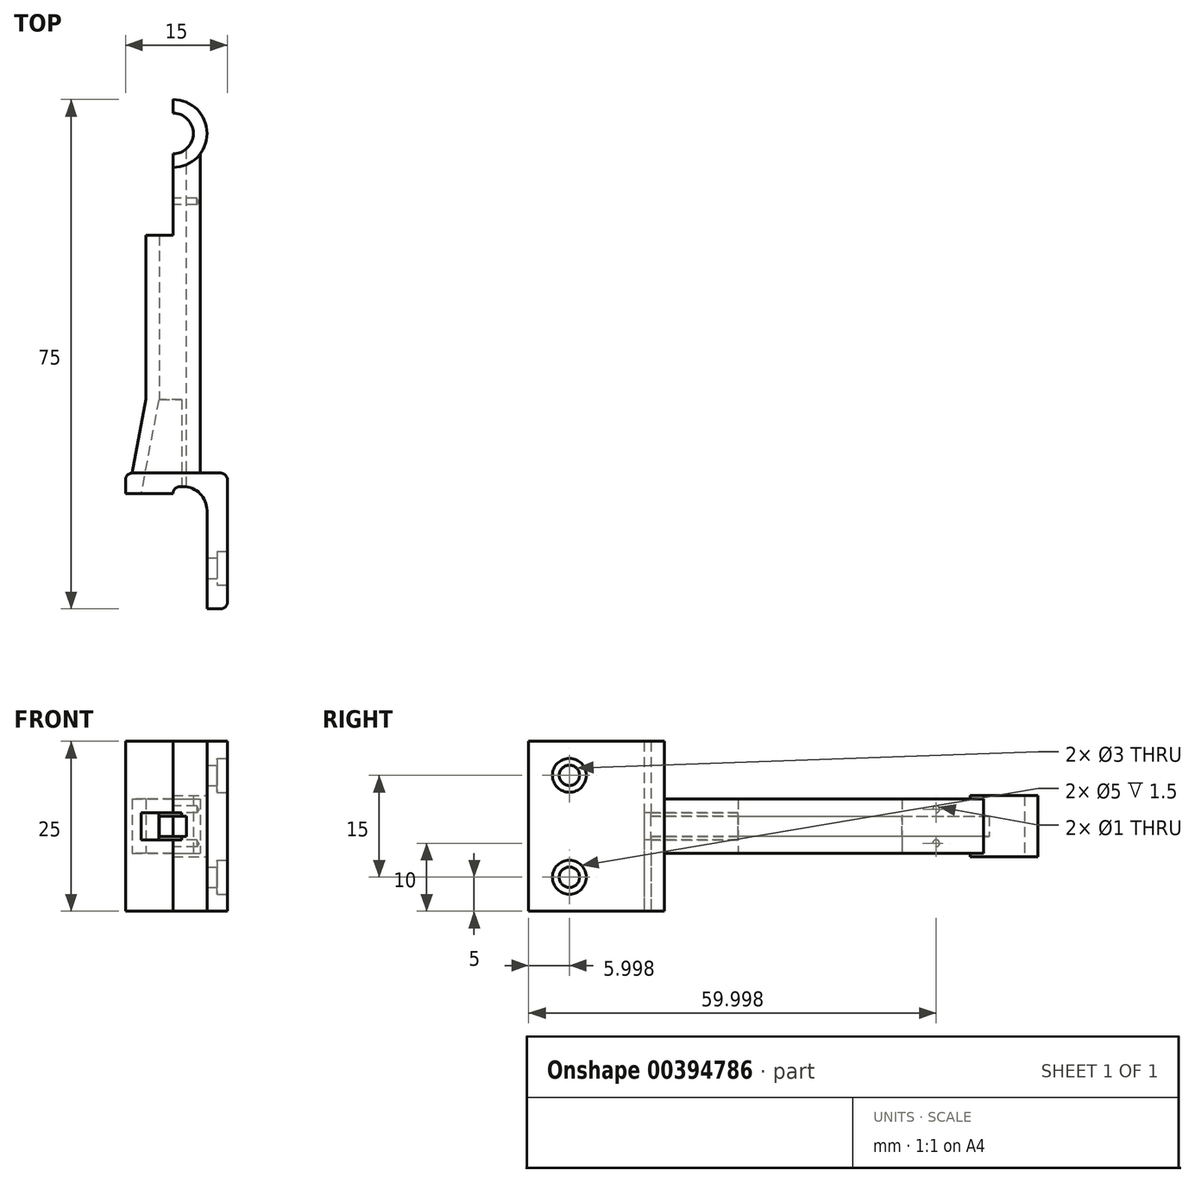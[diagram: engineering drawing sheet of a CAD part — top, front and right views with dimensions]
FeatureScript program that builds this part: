
annotation { "Feature Type Name" : "Feature", "Feature Type Description" : "" }
export const myFeature = defineFeature(function(context is Context, id is Id, definition is map)
    precondition{}
    {
        {
            var Q0;
            Q0=qCreatedBy(makeId("Top.planeOp"),FACE);
            var sketch = newSketch(context, id + "F0", { "sketchPlane" : qUnion([Q0])});
            skLineSegment(sketch, "E0", {"start": v(-8.53, -11.78) * mm, "end": v(4.47, -11.78) * mm});
            skLineSegment(sketch, "E1", {"start": v(5.47, -12.78) * mm, "end": v(5.47, -30.78) * mm});
            skLineSegment(sketch, "E2", {"start": v(4.47, -31.78) * mm, "end": v(2.47, -31.78) * mm});
            skLineSegment(sketch, "E3", {"start": v(2.47, -31.78) * mm, "end": v(2.47, -17.28) * mm});
            skLineSegment(sketch, "E4", {"start": v(-1.03, -13.78) * mm, "end": v(-1.53, -13.78) * mm});
            skLineSegment(sketch, "E5", {"start": v(-2.53, -14.78) * mm, "end": v(-2.53, -14.78) * mm});
            skLineSegment(sketch, "E6", {"start": v(-2.53, -14.78) * mm, "end": v(-9.53, -14.78) * mm});
            skLineSegment(sketch, "E7", {"start": v(-9.53, -14.78) * mm, "end": v(-9.53, -12.78) * mm});
            skPoint(sketch, "E8.visualSharp", {"position": v(2.47, -13.78) * mm});
            skArc(sketch, "E8.filletArc", {"start": v(2.47, -17.28) * mm, "mid": v(1.45, -14.8) * mm, "end": v(-1.03, -13.78) * mm});
            skPoint(sketch, "E9.visualSharp", {"position": v(-2.53, -13.78) * mm});
            skArc(sketch, "E9.filletArc", {"start": v(-1.53, -13.78) * mm, "mid": v(-2.23, -14.08) * mm, "end": v(-2.53, -14.78) * mm});
            skPoint(sketch, "E10.visualSharp", {"position": v(-9.53, -11.78) * mm});
            skArc(sketch, "E10.filletArc", {"start": v(-8.53, -11.78) * mm, "mid": v(-9.23, -12.08) * mm, "end": v(-9.53, -12.78) * mm});
            skPoint(sketch, "E11.visualSharp", {"position": v(5.47, -11.78) * mm});
            skArc(sketch, "E11.filletArc", {"start": v(5.47, -12.78) * mm, "mid": v(5.18, -12.08) * mm, "end": v(4.47, -11.78) * mm});
            skPoint(sketch, "E12.visualSharp", {"position": v(5.47, -31.78) * mm});
            skArc(sketch, "E12.filletArc", {"start": v(4.47, -31.78) * mm, "mid": v(5.18, -31.49) * mm, "end": v(5.47, -30.78) * mm});
            skLineSegment(sketch, "E13", {"start": v(1.47, -11.78) * mm, "end": v(1.47, 35.22) * mm});
            skArc(sketch, "E14", {"start": v(-2.53, 35.22) * mm, "mid": v(0.47, 38.22) * mm, "end": v(-2.53, 41.22) * mm});
            skArc(sketch, "E15", {"start": v(-2.53, 33.22) * mm, "mid": v(2.47, 38.22) * mm, "end": v(-2.53, 43.22) * mm});
            skPoint(sketch, "E16.orphan", {"position": v(1.47, 24.21) * mm});
            skPoint(sketch, "E17.orphan", {"position": v(-6.53, 24.21) * mm});
            skLineSegment(sketch, "E18", {"start": v(-2.53, 43.22) * mm, "end": v(-2.53, 23.22) * mm});
            skLineSegment(sketch, "E19", {"start": v(-2.53, 23.22) * mm, "end": v(-6.53, 23.22) * mm});
            skLineSegment(sketch, "E20", {"start": v(-6.53, 23.22) * mm, "end": v(-6.53, -0.91) * mm});
            skLineSegment(sketch, "E21", {"start": v(-6.53, -0.91) * mm, "end": v(-8.53, -11.78) * mm});
            skLineSegment(sketch, "E22", {"start": v(-6.53, -11.78) * mm, "end": v(-6.53, -11.78) * mm});
            skPoint(sketch, "E23.end.orphan", {"position": v(-4.53, -0.91) * mm});
            skPoint(sketch, "E23.start.orphan", {"position": v(-4.53, 23.22) * mm});
            skSolve(sketch);
        }
        {
            var Q0;
            Q0=makeQuery(id+"F0.imprint","IMPRINT",FACE,{"disambiguationData":[TD([[makeQuery(id+"F0.imprint","IMPRINT",EDGE,{"derivedFrom":sQuery(id+"F0.wireOp",EDGE,"E0")}),-1.0]])]});
            extrude(context, id + "F1", {"entities" : qUnion([Q0]), "endBound" : BoundingType.SYMMETRIC, "depth" : 25 * mm});
        }
        {
            var Q0;
            Q0=makeQuery(id+"F1.opExtrude","SWEPT_FACE",FACE,{"disambiguationData":[OSD([sQuery(id+"F0.wireOp",EDGE,"E1")])]});
            var sketch = newSketch(context, id + "F2", { "sketchPlane" : qUnion([Q0])});
            skPoint(sketch, "E24", {"position": v(-25.78, 7.5) * mm});
            skPoint(sketch, "E25", {"position": v(-25.78, -7.5) * mm});
            skSolve(sketch);
        }
        {
            var Q0;
            Q0=sQuery(id+"F2.wireOp",VERTEX,"E24");
            var Q1;
            Q1=sQuery(id+"F2.wireOp",VERTEX,"E25");
            var Q2;
            Q2=makeQuery(id+"F1.opExtrude","SWEPT_BODY",BODY,{"disambiguationData":[OSD([sQuery(id+"F0.wireOp",EDGE,"E0"),sQuery(id+"F0.wireOp",EDGE,"E1"),sQuery(id+"F0.wireOp",EDGE,"E2"),sQuery(id+"F0.wireOp",EDGE,"E3"),sQuery(id+"F0.wireOp",EDGE,"E4"),sQuery(id+"F0.wireOp",EDGE,"E6"),sQuery(id+"F0.wireOp",EDGE,"E7"),sQuery(id+"F0.wireOp",EDGE,"E8.filletArc"),sQuery(id+"F0.wireOp",EDGE,"E9.filletArc"),sQuery(id+"F0.wireOp",EDGE,"E10.filletArc"),sQuery(id+"F0.wireOp",EDGE,"E11.filletArc"),sQuery(id+"F0.wireOp",EDGE,"E12.filletArc")])]});
            hole(context, id + "F3", {"style" : HoleStyle.C_BORE, "endStyle" : HoleEndStyle.THROUGH, "holeDiameter" : 3 * mm, "cBoreDiameter" : 5 * mm, "cBoreDepth" : 1.5 * mm, "tappedDepth" : 12 * mm, "tapClearance" : 3, "startFromSketch" : true, "locations" : qUnion([Q0, Q1]), "scope" : qUnion([Q2])});
        }
        {
            var Q0;
            {var subQ0=sQuery(id+"F0.wireOp",EDGE,"E13");Q0=makeQuery(id+"F0.imprint","IMPRINT",FACE,{"disambiguationData":[TD([[makeQuery(id+"F0.imprint","IMPRINT",EDGE,{"derivedFrom":subQ0}),1.0]])]});}
            extrude(context, id + "F4", {"entities" : qUnion([Q0]), "operationType" : NewBodyOperationType.ADD, "endBound" : BoundingType.SYMMETRIC, "depth" : 8 * mm});
        }
        {
            var Q0;
            Q0=makeQuery(id+"F0.imprint","IMPRINT",FACE,{"disambiguationData":[TD([[makeQuery(id+"F0.imprint","IMPRINT",EDGE,{"derivedFrom":sQuery(id+"F0.wireOp",EDGE,"E14")}),-1.0]])]});
            extrude(context, id + "F5", {"entities" : qUnion([Q0]), "operationType" : NewBodyOperationType.ADD, "endBound" : BoundingType.SYMMETRIC, "depth" : 9 * mm});
        }
        {
            var Q0;
            Q0=qCreatedBy(makeId("Right.planeOp"),FACE);
            cPlane(context, id + "F6", {"entities" : qUnion([Q0]), "cplaneType" : CPlaneType.OFFSET, "offset" : 2.53 * mm, "oppositeDirection" : true, "width" : 150 * mm, "height" : 150 * mm});
        }
        {
            var Q0;
            Q0=qCreatedBy(id+"F6.planeOp",FACE);
            var sketch = newSketch(context, id + "F7", { "sketchPlane" : qUnion([Q0])});
            skLineSegment(sketch, "E26", {"start": v(36.53, -1.5) * mm, "end": v(-16.2, -1.5) * mm});
            skLineSegment(sketch, "E27", {"start": v(-16.2, 1.5) * mm, "end": v(36.53, 1.5) * mm});
            skLineSegment(sketch, "E28", {"start": v(36.53, 1.5) * mm, "end": v(36.53, -1.5) * mm});
            skLineSegment(sketch, "E29", {"start": v(-16.2, -1.5) * mm, "end": v(-16.2, 1.5) * mm});
            skSolve(sketch);
        }
        {
            var Q0;
            Q0=makeQuery(id+"F7.imprint","IMPRINT",FACE,{"disambiguationData":[TD([[makeQuery(id+"F7.imprint","IMPRINT",EDGE,{"derivedFrom":sQuery(id+"F7.wireOp",EDGE,"E26")}),-1.0]])]});
            extrude(context, id + "F8", {"entities" : qUnion([Q0]), "operationType" : NewBodyOperationType.REMOVE, "endBound" : BoundingType.SYMMETRIC, "oppositeDirection" : true, "depth" : 4 * mm});
        }
        {
            var Q0;
            Q0=qCreatedBy(makeId("Top.planeOp"),FACE);
            var sketch = newSketch(context, id + "F9", { "sketchPlane" : qUnion([Q0])});
            skLineSegment(sketch, "E30", {"start": v(-4.64, -0.95) * mm, "end": v(-7.58, -16.59) * mm});
            skLineSegment(sketch, "E31", {"start": v(-7.58, -16.59) * mm, "end": v(-1.23, -16.59) * mm});
            skLineSegment(sketch, "E32", {"start": v(-1.23, -16.59) * mm, "end": v(-1.23, -0.95) * mm});
            skLineSegment(sketch, "E33", {"start": v(-1.23, -0.95) * mm, "end": v(-4.64, -0.95) * mm});
            skSolve(sketch);
        }
        {
            var Q0;
            Q0=makeQuery(id+"F9.imprint","IMPRINT",FACE,{"disambiguationData":[TD([[makeQuery(id+"F9.imprint","IMPRINT",EDGE,{"derivedFrom":sQuery(id+"F9.wireOp",EDGE,"E30")}),1.0]])]});
            extrude(context, id + "F10", {"entities" : qUnion([Q0]), "operationType" : NewBodyOperationType.REMOVE, "endBound" : BoundingType.SYMMETRIC, "oppositeDirection" : true, "depth" : 4 * mm});
        }
        {
            var Q0;
            {var subQ0=sQuery(id+"F0.wireOp",EDGE,"E18");var subQ2=sQuery(id+"F0.wireOp",EDGE,"E14");Q0=makeQuery(id+"F8.boolean.opBoolean","SPLIT",FACE,{"disambiguationData":[TD([makeQuery(id+"F8.opExtrude","SWEPT_FACE",FACE,{"disambiguationData":[OSD([sQuery(id+"F7.wireOp",EDGE,"E27")])]})])],"derivedFrom":makeQuery(id+"F5.boolean.opBoolean","MERGE",FACE,{"derivedFrom":[makeQuery(id+"F4.opExtrude","SWEPT_FACE",FACE,{"disambiguationData":[OSD([subQ0])]}),makeQuery(id+"F5.opExtrude","SWEPT_FACE",FACE,{"disambiguationData":[OSD([subQ0]),TDD([makeQuery(id+"F0.imprint","IMPRINT",EDGE,{"disambiguationData":[TD([[makeQuery(id+"F0.imprint","INTERSECT",VERTEX,{"disambiguationData":[OD(0.0)],"derivedFrom":[subQ2,subQ0]}),-1.0]])],"derivedFrom":subQ0})])]})]})});}
            var sketch = newSketch(context, id + "F11", { "sketchPlane" : qUnion([Q0])});
            skPoint(sketch, "E34", {"position": v(-28.22, -2.5) * mm});
            skPoint(sketch, "E35", {"position": v(-28.22, 2.5) * mm});
            skSolve(sketch);
        }
        {
            var Q0;
            Q0=sQuery(id+"F11.wireOp",VERTEX,"E34");
            var Q1;
            Q1=sQuery(id+"F11.wireOp",VERTEX,"E35");
            var Q2;
            Q2=makeQuery(id+"F1.opExtrude","SWEPT_BODY",BODY,{"disambiguationData":[OSD([sQuery(id+"F0.wireOp",EDGE,"E0"),sQuery(id+"F0.wireOp",EDGE,"E1"),sQuery(id+"F0.wireOp",EDGE,"E2"),sQuery(id+"F0.wireOp",EDGE,"E3"),sQuery(id+"F0.wireOp",EDGE,"E4"),sQuery(id+"F0.wireOp",EDGE,"E6"),sQuery(id+"F0.wireOp",EDGE,"E7"),sQuery(id+"F0.wireOp",EDGE,"E8.filletArc"),sQuery(id+"F0.wireOp",EDGE,"E9.filletArc"),sQuery(id+"F0.wireOp",EDGE,"E10.filletArc"),sQuery(id+"F0.wireOp",EDGE,"E11.filletArc"),sQuery(id+"F0.wireOp",EDGE,"E12.filletArc")])]});
            hole(context, id + "F12", {"style" : HoleStyle.SIMPLE, "endStyle" : HoleEndStyle.BLIND, "holeDiameter" : 1 * mm, "holeDepth" : 3.5 * mm, "tappedDepth" : 12 * mm, "tapClearance" : 3, "startFromSketch" : true, "locations" : qUnion([Q0, Q1]), "scope" : qUnion([Q2])});
        }
    });
